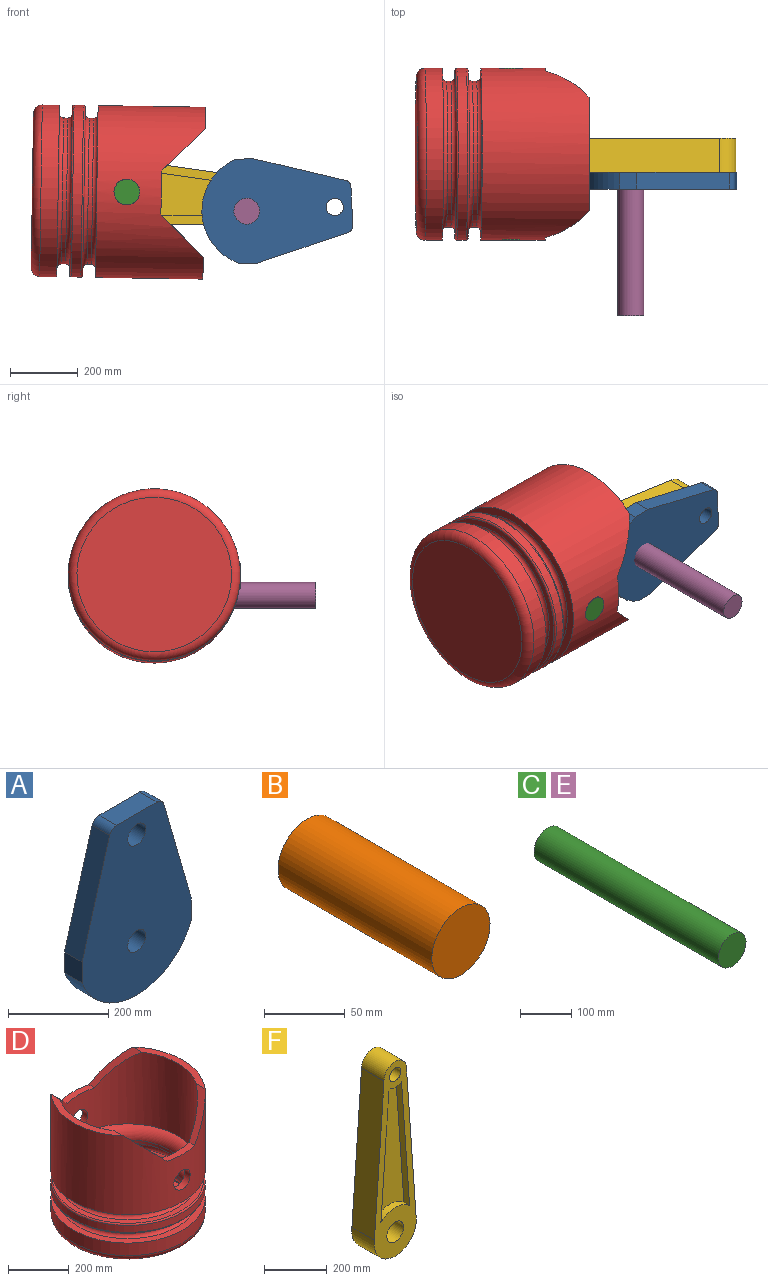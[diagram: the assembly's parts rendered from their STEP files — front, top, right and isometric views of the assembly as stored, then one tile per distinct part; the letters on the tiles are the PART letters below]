
ASSEMBLY  parts=6 mates=7
PART A: 12 faces, bbox 309.3x49.6x443.7 mm
  f0: plane 270.9x77.76mm, normal (-0.96,0,0.28), area 13973.8mm2, adj f1,f7,f8,f10
  f1: plane 50.8x49.58mm, normal (-1,0,0), area 2518.7mm2, adj f0,f2,f7,f8
  f2: cylinder r=165.01mm len=309.14mm, axis (0,1,0), area 19849.7mm2, adj f1,f3,f7,f8
  f3: plane 50.8x49.58mm, normal (1,0,0), area 2518.7mm2, adj f2,f4,f7,f8
  f4: plane 270.94x77.61mm, normal (0.96,0,0.28), area 13973.3mm2, adj f3,f7,f8,f9
  f5: plane 114.66x49.58mm, normal (0,0,1), area 5684.9mm2, adj f7,f8,f9,f10
  f6: cylinder r=25.4mm len=50.8mm, axis (0,1,0), area 7912.7mm2, adj f7,f8
  f7: plane 443.69x309.29mm, normal (0,-1,0), area 100571.4mm2, adj f0,f1,f2,f3,f4,f5,f6,f9
  f8: plane 443.69x309.29mm, normal (0,1,0), area 100571.4mm2, adj f0,f1,f2,f3,f4,f5,f6,f9
  f9: cylinder r=20.34mm len=49.58mm, axis (0,1,0), area 1302.9mm2, adj f4,f5,f7,f8
  f10: cylinder r=20.34mm len=49.58mm, axis (0,1,0), area 1302.3mm2, adj f0,f5,f7,f8
  f11: cylinder r=25.4mm len=50.8mm, axis (0,-1,0), area 7912.7mm2, adj f7,f8
PART B: 3 faces, bbox 50.8x134.3x50.8 mm
  f0: cylinder r=25.4mm len=134.33mm, axis (0,1,0), area 21438.2mm2, adj f1,f2
  f1: plane 50.8x50.8mm, normal (0,-1,0), area 2026.8mm2, adj f0
  f2: plane 50.8x50.8mm, normal (0,1,0), area 2026.8mm2, adj f0
PART C: 3 faces, bbox 76.2x508x76.2 mm
  f0: cylinder r=38.1mm len=508mm, axis (0,1,0), area 121609.8mm2, adj f1,f2
  f1: plane 76.2x76.2mm, normal (0,-1,0), area 4560.4mm2, adj f0
  f2: plane 76.2x76.2mm, normal (0,1,0), area 4560.4mm2, adj f0
PART D: 36 faces, bbox 553.4x553.4x508 mm
  f0: plane 127x127mm, normal (-0.71,0,0.71), area 5587.6mm2, adj f3,f5,f22,f26
  f1: plane 127x34.4mm, normal (0,0,1), area 3264.4mm2, adj f2,f3,f24,f26
  f2: plane 127x127mm, normal (0.71,0,0.71), area 5587.6mm2, adj f1,f3,f4,f26
  f3: cylinder r=254mm len=508mm, axis (0,0,-1), area 428828.2mm2, adj f0,f1,f2,f4,f5,f6,f22,f23
  f4: plane 336.01x63.5mm, normal (0,0,1), area 8088.4mm2, adj f2,f3,f23,f26
  f5: plane 336.01x63.5mm, normal (0,0,1), area 8088.4mm2, adj f0,f3,f24,f26
  f6: plane 508x508mm, normal (0,0,-1), area 38509.8mm2, adj f3,f18
  f7: plane 497.84x497.84mm, normal (0,0,1), area 30483.5mm2, adj f17,f21
  f8: cylinder r=215.9mm len=431.8mm, axis (0,0,1), area 17228.1mm2, adj f17,f18
  f9: cylinder r=254mm len=508mm, axis (0,0,-1), area 44590.3mm2, adj f20,f21
  f10: plane 497.84x497.84mm, normal (0,0,-1), area 30483.5mm2, adj f16,f20
  f11: plane 508x508mm, normal (0,0,1), area 38509.8mm2, adj f14,f15
  f12: cylinder r=215.9mm len=431.8mm, axis (0,0,1), area 17228.1mm2, adj f15,f16
  f13: plane 457.2x457.2mm, normal (0,0,-1), area 164173.2mm2, adj f19
  f14: cylinder r=254mm len=508mm, axis (0,0,-1), area 81073.2mm2, adj f11,f19
  f15: torus R=228.6mm, axis (0,0,-1), area 27640.2mm2, adj f11,f12
  f16: torus R=228.6mm, axis (0,0,-1), area 27640.2mm2, adj f10,f12
  f17: torus R=228.6mm, axis (0,0,-1), area 27640.2mm2, adj f7,f8
  f18: torus R=228.6mm, axis (0,0,-1), area 27640.2mm2, adj f6,f8
  f19: torus R=228.6mm, axis (0,0,1), area 61360.9mm2, adj f13,f14
  f20: torus R=248.92mm, axis (0,0,-1), area 12642.4mm2, adj f9,f10
  f21: torus R=248.92mm, axis (0,0,-1), area 12642.4mm2, adj f7,f9
  f22: plane 127x34.4mm, normal (0,0,1), area 3264.4mm2, adj f0,f3,f23,f26
  f23: plane 127x127mm, normal (0.71,0,0.71), area 5587.6mm2, adj f3,f4,f22,f26
  f24: plane 127x127mm, normal (-0.71,0,0.71), area 5587.6mm2, adj f1,f3,f5,f26
  f25: torus R=228.6mm, axis (0,0,-1), area 46309mm2, adj f27,f32
  f26: cylinder r=228.6mm len=457.2mm, axis (0,0,-1), area 340349.1mm2, adj f0,f1,f2,f4,f5,f22,f23,f24
  f27: cylinder r=190.5mm len=381mm, axis (0,0,1), area 15201.2mm2, adj f25,f33
  f28: cylinder r=190.5mm len=381mm, axis (0,0,1), area 15201.2mm2, adj f31,f32
  f29: plane 457.2x457.2mm, normal (0,0,1), area 164173.2mm2, adj f30
  f30: cylinder r=228.6mm len=457.2mm, axis (0,0,-1), area 36482.9mm2, adj f29,f31
  f31: torus R=228.6mm, axis (0,0,-1), area 76840.2mm2, adj f28,f30
  f32: torus R=228.6mm, axis (0,0,-1), area 46309mm2, adj f25,f28
  f33: torus R=228.6mm, axis (0,0,-1), area 76840.2mm2, adj f26,f27
  f34: cylinder r=38.1mm len=76.2mm, axis (0,-1,0), area 6119mm2, adj f3,f26
  f35: cylinder r=38.1mm len=76.2mm, axis (0,-1,0), area 6119.1mm2, adj f3,f26
PART E: same geometry as C
PART F: 18 faces, bbox 190.5x101.6x762 mm
  f0: plane 762x190.5mm, normal (0,-1,0), area 57346.6mm2, adj f1,f2,f3,f4,f5,f6,f13,f14
  f1: cylinder r=95.25mm len=190.5mm, axis (0,1,0), area 33191.1mm2, adj f0,f2,f5,f7
  f2: plane 602.27x101.6mm, normal (1,0,0.07), area 61350.1mm2, adj f0,f1,f3,f7
  f3: cylinder r=50.8mm len=101.6mm, axis (0,1,0), area 16214.6mm2, adj f0,f2,f5,f7
  f4: cylinder r=25.4mm len=101.6mm, axis (0,1,0), area 16214.6mm2, adj f0,f7
  f5: plane 602.27x101.6mm, normal (-1,0,0.07), area 61350.1mm2, adj f0,f1,f3,f7
  f6: cylinder r=38.1mm len=101.6mm, axis (0,1,0), area 24322mm2, adj f0,f7
  f7: plane 762x190.5mm, normal (0,1,0), area 57346.6mm2, adj f1,f2,f3,f4,f5,f6,f8,f9
  f8: cylinder r=50.8mm len=56.75mm, axis (0,1,0), area 1529.4mm2, adj f7,f9,f11,f12
  f9: plane 503.95x36.37mm, normal (1,0,-0.07), area 12833.6mm2, adj f7,f8,f10,f12
  f10: cylinder r=95.25mm len=129.48mm, axis (0,1,0), area 3616.3mm2, adj f7,f9,f11,f12
  f11: plane 503.95x36.37mm, normal (-1,0,-0.07), area 12833.6mm2, adj f7,f8,f10,f12
  f12: plane 503.95x129.48mm, normal (0,1,0), area 44335.1mm2, adj f8,f9,f10,f11
  f13: cylinder r=50.8mm len=56.75mm, axis (0,-1,0), area 1529.4mm2, adj f0,f14,f16,f17
  f14: plane 503.95x36.37mm, normal (1,0,-0.07), area 12833.6mm2, adj f0,f13,f15,f17
  f15: cylinder r=95.25mm len=129.48mm, axis (0,-1,0), area 3616.3mm2, adj f0,f14,f16,f17
  f16: plane 503.95x36.37mm, normal (-1,0,-0.07), area 12833.6mm2, adj f0,f13,f15,f17
  f17: plane 503.95x129.48mm, normal (0,-1,0), area 44335.1mm2, adj f13,f14,f15,f16
PLACE A rot(axis=(0,1,0),87.2deg) t=(0,-84.75,0)mm
PLACE B at identity fixed
PLACE C rot(axis=(0,-1,0),25.6deg) t=(-354.39,223.21,56.93)mm
PLACE D rot(axis=(0,1,0),90.9deg) t=(-633.76,-30.79,61.16)mm
PLACE E at identity
PLACE F rot(axis=(0,1,0),94.1deg) t=(206.12,16.85,16.4)mm
MATE cylindrical A.f6 <-> B.f0  axis (0,1,0) through (0,-134.33,0)mm
MATE planar F.f4 <-> A.f11  axis (0,-1,0) through (259.95,-84.75,12.51)mm
MATE cylindrical F.f6 <-> C.f0  axis (0,1,0) through (-354.39,-33.95,56.93)mm
MATE cylindrical F.f4 <-> A.f11  axis (0,1,0) through (259.95,16.85,12.51)mm
MATE cylindrical C.f0 <-> D.f34  axis (0,1,0) through (-354.39,-284.79,56.93)mm
MATE cylindrical F.f4 <-> A.f11  axis (0,1,0) through (259.95,-84.75,12.51)mm
MATE planar B.f0 <-> A.f7  axis (0,-1,0) through (0,-134.33,0)mm
